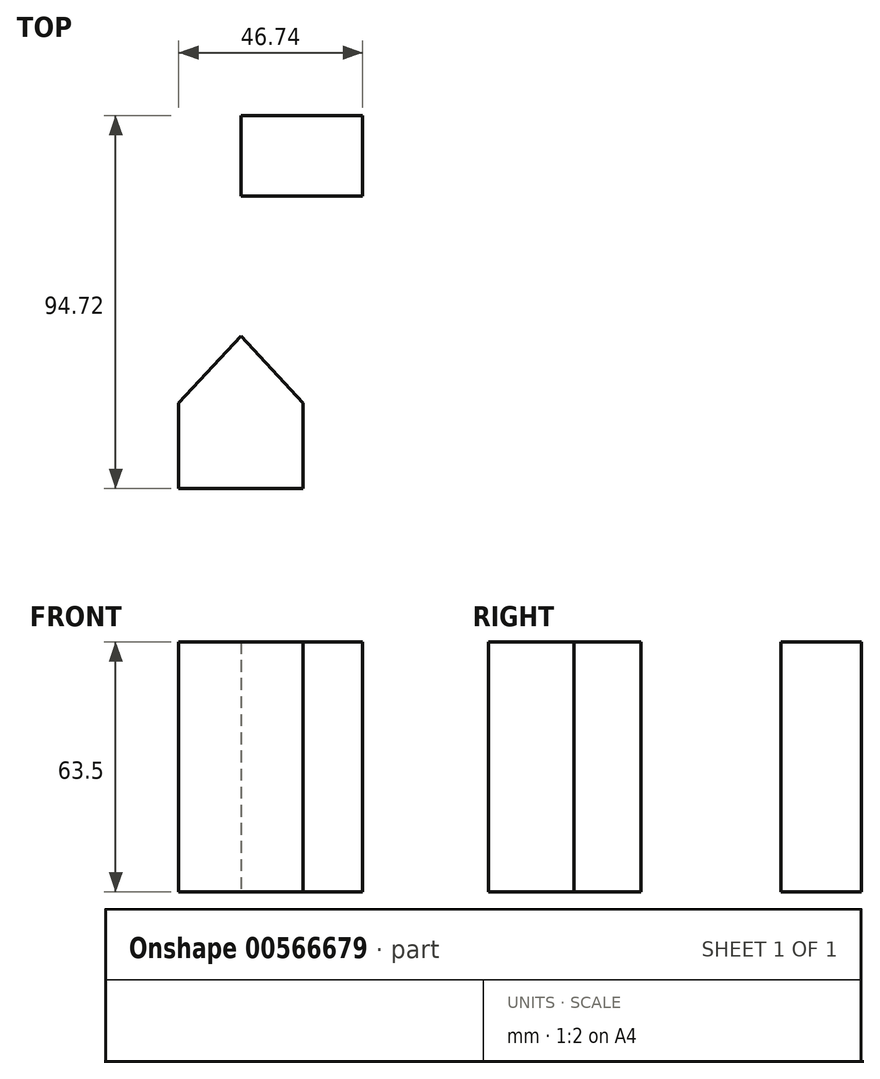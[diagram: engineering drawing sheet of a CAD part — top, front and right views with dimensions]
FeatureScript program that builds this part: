
annotation { "Feature Type Name" : "Feature", "Feature Type Description" : "" }
export const myFeature = defineFeature(function(context is Context, id is Id, definition is map)
    precondition{}
    {
        {
            var Q0;
            Q0=qCreatedBy(makeId("Top.planeOp"),FACE);
            var sketch = newSketch(context, id + "F0", { "sketchPlane" : qUnion([Q0])});
            skLineSegment(sketch, "E0.bottom", {"start": v(-24.45, 30.49) * mm, "end": v(-55.4, 30.49) * mm});
            skLineSegment(sketch, "E0.top", {"start": v(-24.45, 50.92) * mm, "end": v(-55.4, 50.92) * mm});
            skLineSegment(sketch, "E0.left", {"start": v(-24.45, 30.49) * mm, "end": v(-24.45, 50.92) * mm});
            skLineSegment(sketch, "E0.right", {"start": v(-55.4, 30.49) * mm, "end": v(-55.4, 50.92) * mm});
            skPoint(sketch, "E0.middle", {"position": v(-39.93, 40.7) * mm});
            skLineSegment(sketch, "E1.bottom", {"start": v(-39.62, -43.8) * mm, "end": v(-71.19, -43.8) * mm});
            skLineSegment(sketch, "E1.left", {"start": v(-39.62, -43.8) * mm, "end": v(-39.62, -22.13) * mm});
            skLineSegment(sketch, "E1.right", {"start": v(-71.19, -43.8) * mm, "end": v(-71.19, -22.13) * mm});
            skPoint(sketch, "E1.middle", {"position": v(-55.4, -32.96) * mm});
            skLineSegment(sketch, "E2", {"start": v(-39.62, -22.13) * mm, "end": v(-55.4, -5.1) * mm});
            skLineSegment(sketch, "E3", {"start": v(-71.19, -22.13) * mm, "end": v(-55.4, -5.1) * mm});
            skSolve(sketch);
        }
        {
            var Q0;
            Q0 = qSketchRegion(id + "F0", true);
            extrude(context, id + "F1", {"entities" : qUnion([Q0]), "depth" : 63.5 * mm, "offsetDistance" : 25.4 * mm});
        }
    });
